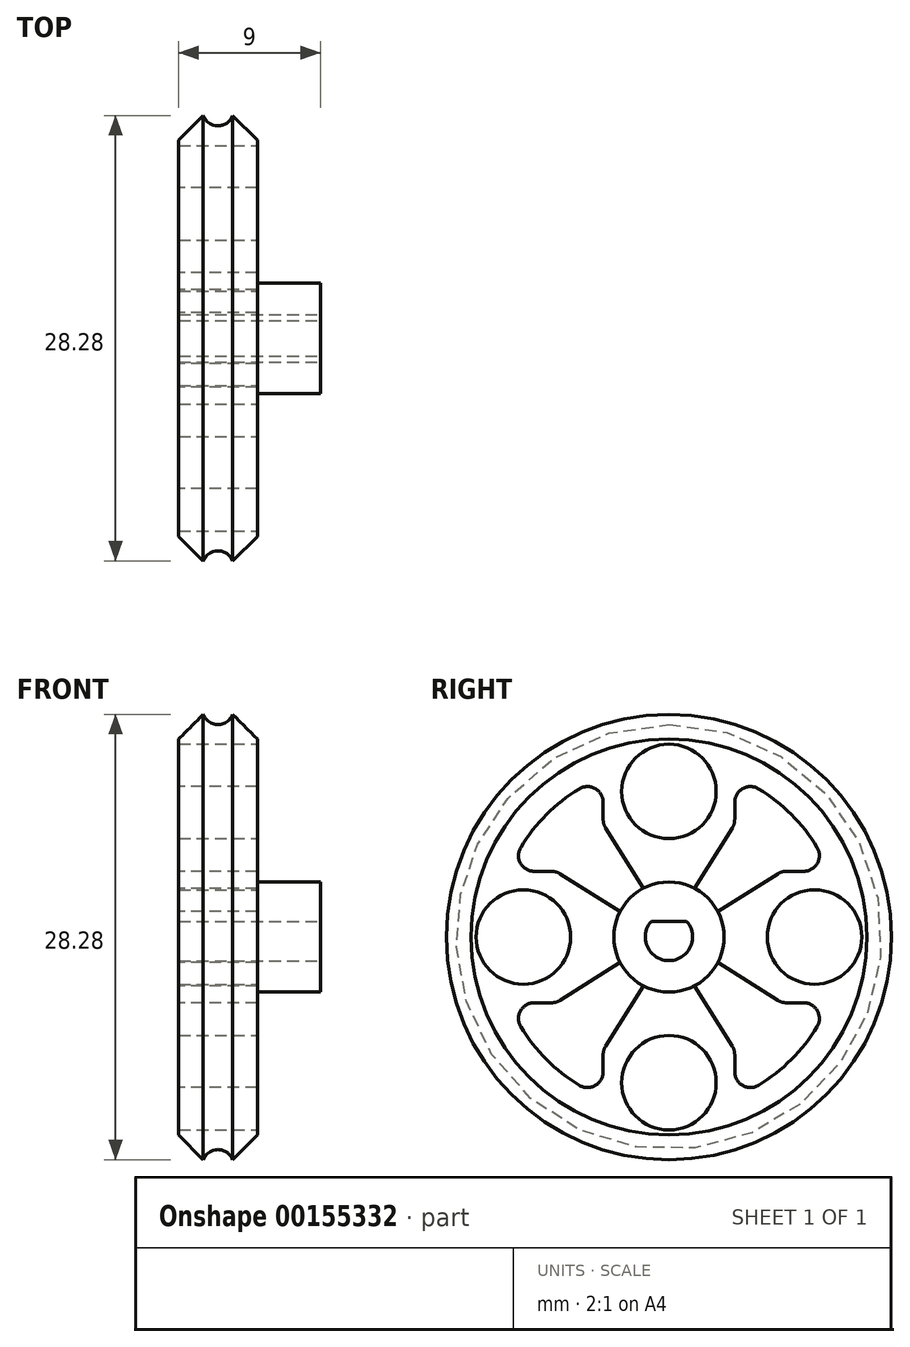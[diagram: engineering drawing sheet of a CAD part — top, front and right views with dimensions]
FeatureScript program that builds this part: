
annotation { "Feature Type Name" : "Feature", "Feature Type Description" : "" }
export const myFeature = defineFeature(function(context is Context, id is Id, definition is map)
    precondition{}
    {
        {
            var Q0;
            Q0=qCreatedBy(makeId("Top.planeOp"),FACE);
            var sketch = newSketch(context, id + "F0", { "sketchPlane" : qUnion([Q0])});
            skLineSegment(sketch, "E0", {"start": v(-2.5, 0) * mm, "end": v(-2.5, 12.57) * mm});
            skLineSegment(sketch, "E1", {"start": v(-2.5, 12.57) * mm, "end": v(-0.93, 14.14) * mm});
            skArc(sketch, "E2", {"start": v(-0.93, 14.14) * mm, "mid": v(0, 13.5) * mm, "end": v(0.93, 14.14) * mm});
            skLineSegment(sketch, "E3", {"start": v(-2.5, 0) * mm, "end": v(6.5, 0) * mm});
            skLineSegment(sketch, "E4", {"start": v(6.5, 0) * mm, "end": v(6.5, 3.5) * mm});
            skLineSegment(sketch, "E5", {"start": v(6.5, 3.5) * mm, "end": v(2.5, 3.5) * mm});
            skLineSegment(sketch, "E6", {"start": v(2.5, 3.5) * mm, "end": v(2.5, 12.57) * mm});
            skLineSegment(sketch, "E7", {"start": v(2.5, 12.57) * mm, "end": v(0.93, 14.14) * mm});
            skSolve(sketch);
        }
        {
            var Q0;
            Q0 = qSketchRegion(id + "F0", true);
            var Q1;
            Q1=sQuery(id+"F0.wireOp",EDGE,"E3");
            revolve(context, id + "F1", {"entities" : qUnion([Q0]), "axis" : qUnion([Q1]), "revolveType" : RevolveType.FULL});
        }
        {
            var Q0;
            Q0=makeQuery(id+"F1.opRevolve","SWEPT_FACE",FACE,{"disambiguationData":[OSD([sQuery(id+"F0.wireOp",EDGE,"E0")])]});
            var sketch = newSketch(context, id + "F2", { "sketchPlane" : qUnion([Q0])});
            skArc(sketch, "E8", {"start": v(-4.18, 10.18) * mm, "mid": v(-7.78, 7.78) * mm, "end": v(-10.18, 4.18) * mm});
            skLineSegment(sketch, "E9.bottom", {"start": v(4.18, 10.18) * mm, "end": v(4.18, 10.18) * mm});
            skLineSegment(sketch, "E9.left", {"start": v(-4.18, 10.18) * mm, "end": v(-4.18, 7.18) * mm});
            skLineSegment(sketch, "E9.right", {"start": v(4.18, 10.18) * mm, "end": v(4.18, 7.18) * mm});
            skLineSegment(sketch, "E10.bottom", {"start": v(-10.18, 4.18) * mm, "end": v(-7.18, 4.18) * mm});
            skLineSegment(sketch, "E10.top", {"start": v(-10.18, -4.18) * mm, "end": v(-7.18, -4.18) * mm});
            skLineSegment(sketch, "E11.trimOffspring", {"start": v(7.18, 4.18) * mm, "end": v(10.18, 4.18) * mm});
            skLineSegment(sketch, "E12.trimOffspring", {"start": v(7.18, -4.18) * mm, "end": v(10.18, -4.18) * mm});
            skLineSegment(sketch, "E13.trimOffspring", {"start": v(4.18, -7.18) * mm, "end": v(4.18, -10.18) * mm});
            skLineSegment(sketch, "E14.trimOffspring", {"start": v(-4.18, -7.18) * mm, "end": v(-4.18, -10.18) * mm});
            skArc(sketch, "E15.trimOffspring", {"start": v(-10.18, -4.18) * mm, "mid": v(-7.78, -7.78) * mm, "end": v(-4.18, -10.18) * mm});
            skArc(sketch, "E16.trimOffspring", {"start": v(10.18, 4.18) * mm, "mid": v(7.78, 7.78) * mm, "end": v(4.18, 10.18) * mm});
            skArc(sketch, "E17.trimOffspring", {"start": v(4.18, -10.18) * mm, "mid": v(7.78, -7.78) * mm, "end": v(10.18, -4.18) * mm});
            skLineSegment(sketch, "E18", {"start": v(4.18, 7.18) * mm, "end": v(1.62, 3.1) * mm});
            skLineSegment(sketch, "E19", {"start": v(7.18, 4.18) * mm, "end": v(3.1, 1.62) * mm});
            skLineSegment(sketch, "E20", {"start": v(-4.18, 7.18) * mm, "end": v(-1.62, 3.1) * mm});
            skLineSegment(sketch, "E21", {"start": v(-7.18, 4.18) * mm, "end": v(-3.1, 1.62) * mm});
            skLineSegment(sketch, "E22", {"start": v(7.18, -4.18) * mm, "end": v(3.1, -1.62) * mm});
            skLineSegment(sketch, "E23", {"start": v(4.18, -7.18) * mm, "end": v(1.62, -3.1) * mm});
            skLineSegment(sketch, "E24", {"start": v(-4.18, -7.18) * mm, "end": v(-1.62, -3.1) * mm});
            skLineSegment(sketch, "E25", {"start": v(-7.18, -4.18) * mm, "end": v(-3.1, -1.62) * mm});
            skPoint(sketch, "E26.orphan", {"position": v(4.18, 4.18) * mm});
            skPoint(sketch, "E27.orphan", {"position": v(4.18, -4.18) * mm});
            skPoint(sketch, "E28.orphan", {"position": v(-4.18, -4.18) * mm});
            skPoint(sketch, "E29.orphan", {"position": v(-4.18, 4.18) * mm});
            skArc(sketch, "E30.0", {"start": v(-3.1, -1.62) * mm, "mid": v(-2.47, -2.47) * mm, "end": v(-1.62, -3.1) * mm});
            skArc(sketch, "E31.0.0", {"start": v(-1.62, 3.1) * mm, "mid": v(-2.47, 2.47) * mm, "end": v(-3.1, 1.62) * mm});
            skArc(sketch, "E32.trimOffspring", {"start": v(1.62, -3.1) * mm, "mid": v(2.47, -2.47) * mm, "end": v(3.1, -1.62) * mm});
            skArc(sketch, "E33.trimOffspring", {"start": v(3.1, 1.62) * mm, "mid": v(2.47, 2.47) * mm, "end": v(1.62, 3.1) * mm});
            skSolve(sketch);
        }
        {
            var Q0;
            Q0 = qSketchRegion(id + "F2", true);
            extrude(context, id + "F3", {"entities" : qUnion([Q0]), "operationType" : NewBodyOperationType.REMOVE, "oppositeDirection" : true, "depth" : 25 * mm});
        }
        {
            var Q0;
            Q0=makeQuery(id+"F1.opRevolve","SWEPT_FACE",FACE,{"disambiguationData":[OSD([sQuery(id+"F0.wireOp",EDGE,"E4")])]});
            var sketch = newSketch(context, id + "F4", { "sketchPlane" : qUnion([Q0])});
            skArc(sketch, "E34", {"start": v(-1.12, 1) * mm, "mid": v(0, -1.5) * mm, "end": v(1.12, 1) * mm});
            skLineSegment(sketch, "E35", {"start": v(-1.12, 1) * mm, "end": v(1.12, 1) * mm});
            skSolve(sketch);
        }
        {
            var Q0;
            Q0 = qSketchRegion(id + "F4", true);
            extrude(context, id + "F5", {"entities" : qUnion([Q0]), "operationType" : NewBodyOperationType.REMOVE, "oppositeDirection" : true, "depth" : 25 * mm});
        }
        {
            var Q0;
            Q0=makeQuery(id+"F3.boolean.opBoolean","COPY",EDGE,{"derivedFrom":makeQuery(id+"F3.opExtrude","SWEPT_EDGE",EDGE,{"disambiguationData":[OSD([sQuery(id+"F2.wireOp",EDGE,"E9.right"),sQuery(id+"F2.wireOp",EDGE,"E11.trimOffspring")])]})});
            var Q1;
            Q1=makeQuery(id+"F3.boolean.opBoolean","COPY",EDGE,{"derivedFrom":makeQuery(id+"F3.opExtrude","SWEPT_EDGE",EDGE,{"disambiguationData":[OSD([sQuery(id+"F2.wireOp",EDGE,"E9.left"),sQuery(id+"F2.wireOp",EDGE,"E10.bottom")])]})});
            var Q2;
            Q2=makeQuery(id+"F3.boolean.opBoolean","COPY",EDGE,{"derivedFrom":makeQuery(id+"F3.opExtrude","SWEPT_EDGE",EDGE,{"disambiguationData":[OSD([sQuery(id+"F2.wireOp",EDGE,"E10.top"),sQuery(id+"F2.wireOp",EDGE,"E14.trimOffspring")])]})});
            var Q3;
            Q3=makeQuery(id+"F3.boolean.opBoolean","COPY",EDGE,{"derivedFrom":makeQuery(id+"F3.opExtrude","SWEPT_EDGE",EDGE,{"disambiguationData":[OSD([sQuery(id+"F2.wireOp",EDGE,"E12.trimOffspring"),sQuery(id+"F2.wireOp",EDGE,"E13.trimOffspring")])]})});
            var Q4;
            Q4=makeQuery(id+"F3.boolean.opBoolean","COPY",EDGE,{"derivedFrom":makeQuery(id+"F3.opExtrude","SWEPT_EDGE",EDGE,{"disambiguationData":[OSD([sQuery(id+"F2.wireOp",EDGE,"E11.trimOffspring"),sQuery(id+"F2.wireOp",EDGE,"E16.trimOffspring")])]})});
            var Q5;
            Q5=makeQuery(id+"F3.boolean.opBoolean","COPY",EDGE,{"derivedFrom":makeQuery(id+"F3.opExtrude","SWEPT_EDGE",EDGE,{"disambiguationData":[OSD([sQuery(id+"F2.wireOp",EDGE,"E14.trimOffspring"),sQuery(id+"F2.wireOp",EDGE,"E15.trimOffspring")])]})});
            var Q6;
            Q6=makeQuery(id+"F3.boolean.opBoolean","COPY",EDGE,{"derivedFrom":makeQuery(id+"F3.opExtrude","SWEPT_EDGE",EDGE,{"disambiguationData":[OSD([sQuery(id+"F2.wireOp",EDGE,"E13.trimOffspring"),sQuery(id+"F2.wireOp",EDGE,"E17.trimOffspring")])]})});
            var Q7;
            Q7=makeQuery(id+"F3.boolean.opBoolean","COPY",EDGE,{"derivedFrom":makeQuery(id+"F3.opExtrude","SWEPT_EDGE",EDGE,{"disambiguationData":[OSD([sQuery(id+"F2.wireOp",EDGE,"E12.trimOffspring"),sQuery(id+"F2.wireOp",EDGE,"E17.trimOffspring")])]})});
            var Q8;
            Q8=makeQuery(id+"F3.boolean.opBoolean","COPY",EDGE,{"derivedFrom":makeQuery(id+"F3.opExtrude","SWEPT_EDGE",EDGE,{"disambiguationData":[OSD([sQuery(id+"F2.wireOp",EDGE,"E10.top"),sQuery(id+"F2.wireOp",EDGE,"E15.trimOffspring")])]})});
            var Q9;
            Q9=makeQuery(id+"F3.boolean.opBoolean","COPY",EDGE,{"derivedFrom":makeQuery(id+"F3.opExtrude","SWEPT_EDGE",EDGE,{"disambiguationData":[OSD([sQuery(id+"F2.wireOp",EDGE,"E8"),sQuery(id+"F2.wireOp",EDGE,"E10.bottom")])]})});
            var Q10;
            Q10=makeQuery(id+"F3.boolean.opBoolean","COPY",EDGE,{"derivedFrom":makeQuery(id+"F3.opExtrude","SWEPT_EDGE",EDGE,{"disambiguationData":[OSD([sQuery(id+"F2.wireOp",EDGE,"E8"),sQuery(id+"F2.wireOp",EDGE,"E9.left")])]})});
            var Q11;
            Q11=makeQuery(id+"F3.boolean.opBoolean","COPY",EDGE,{"derivedFrom":makeQuery(id+"F3.opExtrude","SWEPT_EDGE",EDGE,{"disambiguationData":[OSD([sQuery(id+"F2.wireOp",EDGE,"E9.right"),sQuery(id+"F2.wireOp",EDGE,"E16.trimOffspring")])]})});
            fillet(context, id + "F6", {"entities" : qUnion([Q0, Q1, Q2, Q3, Q4, Q5, Q6, Q7, Q8, Q9, Q10, Q11]), "radius" : 1 * mm, "tangentPropagation" : true, "allowEdgeOverflow" : false});
        }
        {
            var Q0;
            Q0=makeQuery(id+"F1.opRevolve","SWEPT_FACE",FACE,{"disambiguationData":[OSD([sQuery(id+"F0.wireOp",EDGE,"E6")])]});
            var sketch = newSketch(context, id + "F7", { "sketchPlane" : qUnion([Q0])});
            skCircle(sketch, "E36", {"center": v(0, 9.25) * mm, "radius": 3 * mm});
            skCircle(sketch, "E37", {"center": v(-9.25, 0) * mm, "radius": 3 * mm});
            skCircle(sketch, "E38", {"center": v(9.25, 0) * mm, "radius": 3 * mm});
            skCircle(sketch, "E39", {"center": v(0, -9.25) * mm, "radius": 3 * mm});
            skCircle(sketch, "E40", {"center": v(0, 0) * mm, "radius": 9.25 * mm, "construction": true});
            skSolve(sketch);
        }
        {
            var Q0;
            Q0 = qSketchRegion(id + "F7", true);
            extrude(context, id + "F8", {"entities" : qUnion([Q0]), "operationType" : NewBodyOperationType.REMOVE, "oppositeDirection" : true, "depth" : 25 * mm});
        }
    });
